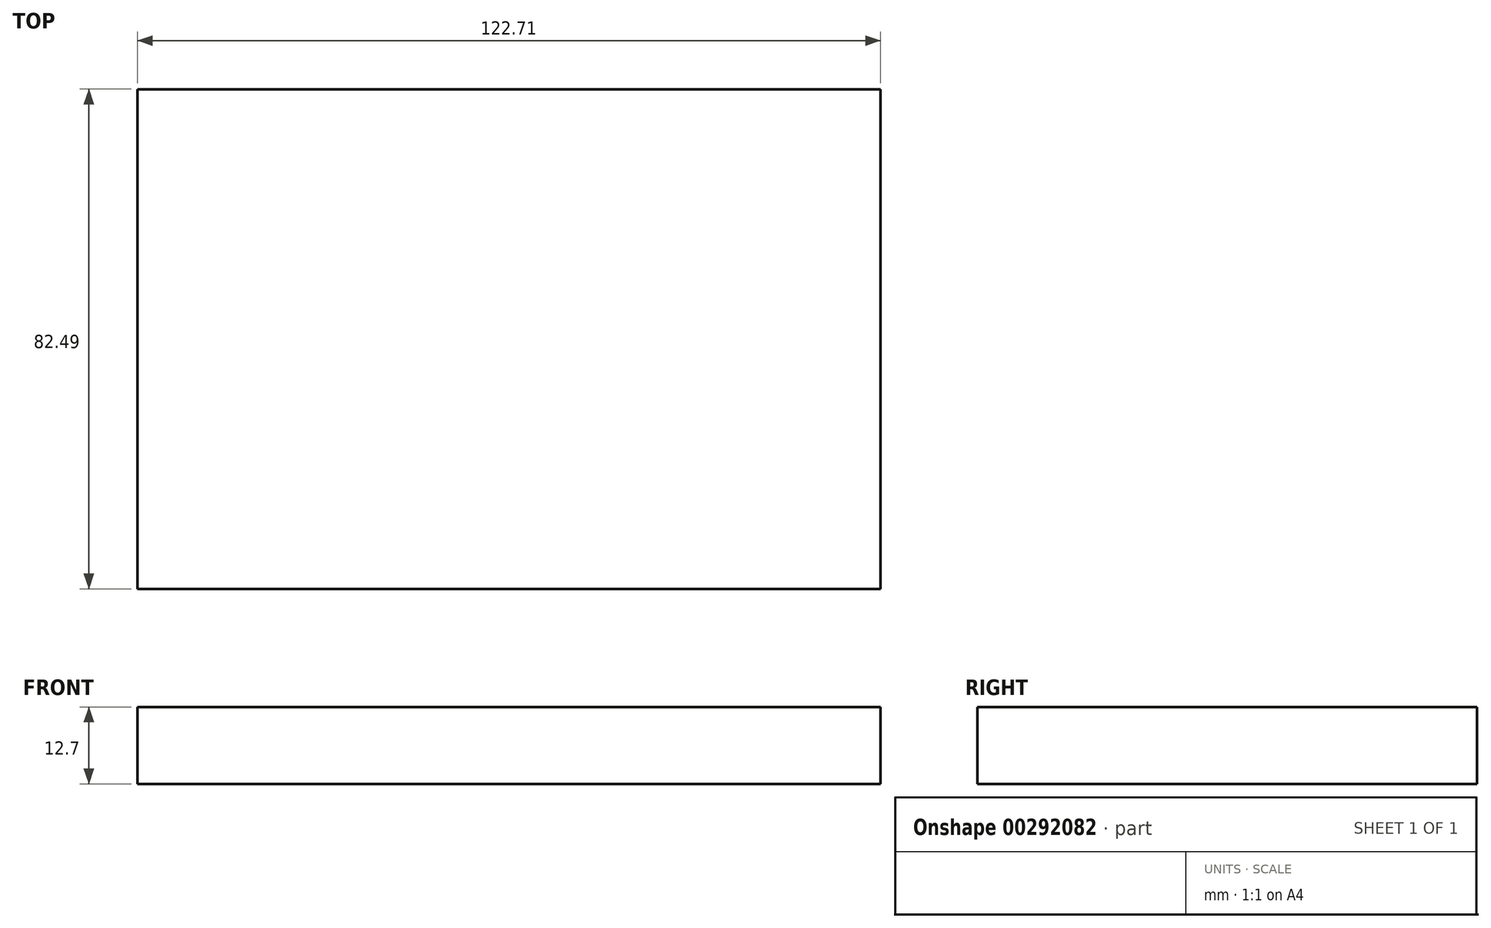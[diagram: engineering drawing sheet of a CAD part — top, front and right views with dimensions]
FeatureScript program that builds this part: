
annotation { "Feature Type Name" : "Feature", "Feature Type Description" : "" }
export const myFeature = defineFeature(function(context is Context, id is Id, definition is map)
    precondition{}
    {
        {
            var Q0;
            Q0=qCreatedBy(makeId("Top.planeOp"),FACE);
            var sketch = newSketch(context, id + "F0", { "sketchPlane" : qUnion([Q0])});
            skLineSegment(sketch, "E0.bottom", {"start": v(-88.32, 36) * mm, "end": v(34.4, 36) * mm});
            skLineSegment(sketch, "E0.top", {"start": v(-88.32, -46.5) * mm, "end": v(34.4, -46.5) * mm});
            skLineSegment(sketch, "E0.left", {"start": v(-88.32, 36) * mm, "end": v(-88.32, -46.5) * mm});
            skLineSegment(sketch, "E0.right", {"start": v(34.4, 36) * mm, "end": v(34.4, -46.5) * mm});
            skSolve(sketch);
        }
        {
            var Q0;
            Q0=makeQuery(id+"F0.imprint","IMPRINT",FACE,{"disambiguationData":[TD([[makeQuery(id+"F0.imprint","IMPRINT",EDGE,{"derivedFrom":sQuery(id+"F0.wireOp",EDGE,"E0.bottom")}),-1.0]])]});
            extrude(context, id + "F1", {"entities" : qUnion([Q0]), "depth" : 12.7 * mm});
        }
    });
